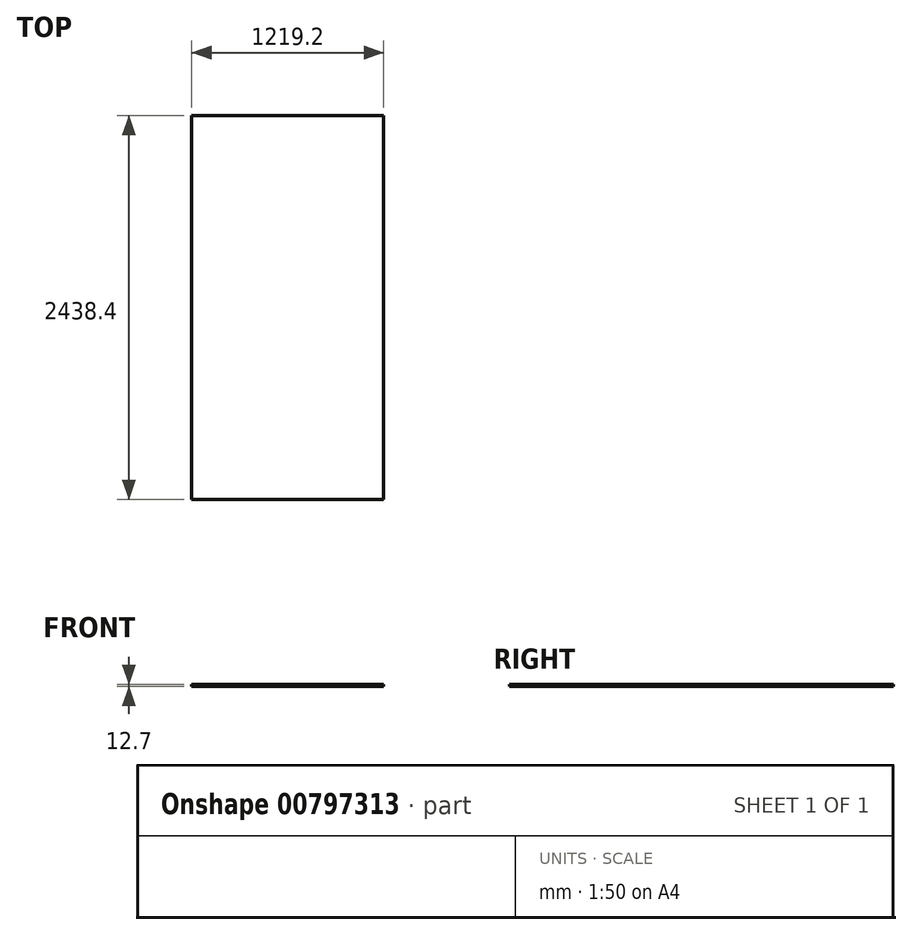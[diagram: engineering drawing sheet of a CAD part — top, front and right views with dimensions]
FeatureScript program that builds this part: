
annotation { "Feature Type Name" : "Feature", "Feature Type Description" : "" }
export const myFeature = defineFeature(function(context is Context, id is Id, definition is map)
    precondition{}
    {
        {
            var Q0;
            Q0=qCreatedBy(makeId("Top.planeOp"),FACE);
            var sketch = newSketch(context, id + "F0", { "sketchPlane" : qUnion([Q0])});
            skLineSegment(sketch, "E0.bottom", {"start": v(-609.6, 1219.2) * mm, "end": v(609.6, 1219.2) * mm});
            skLineSegment(sketch, "E0.top", {"start": v(-609.6, -1219.2) * mm, "end": v(609.6, -1219.2) * mm});
            skLineSegment(sketch, "E0.left", {"start": v(-609.6, 1219.2) * mm, "end": v(-609.6, -1219.2) * mm});
            skLineSegment(sketch, "E0.right", {"start": v(609.6, 1219.2) * mm, "end": v(609.6, -1219.2) * mm});
            skPoint(sketch, "E0.middle", {"position": v(0, 0) * mm});
            skSolve(sketch);
        }
        {
            var Q0;
            Q0 = qSketchRegion(id + "F0", true);
            extrude(context, id + "F1", {"entities" : qUnion([Q0]), "depth" : 12.7 * mm, "offsetDistance" : 25 * mm});
        }
    });
